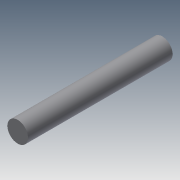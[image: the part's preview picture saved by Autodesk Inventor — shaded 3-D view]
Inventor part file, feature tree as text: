
AUTODESK INVENTOR PART (.ipt)
format: ipt  version: 2013 (Build 170138000, 138)  size: 66,048 bytes
history: native  units: mm
features: extrude x1, sketch x1
ambient origin geometry x8: Origin, YZ Plane, XZ Plane, XY Plane, X Axis, Y Axis, Z Axis, Center Point
bodies: Solid1 (feature_tree)
feature tree (2):
  extrude  "Extrusion1"  Depth=28.0mm TaperAngle=0.0deg
  sketch  "Sketch1"  dims[d0=4.0mm d1=28.0mm d2=0.0mm]
